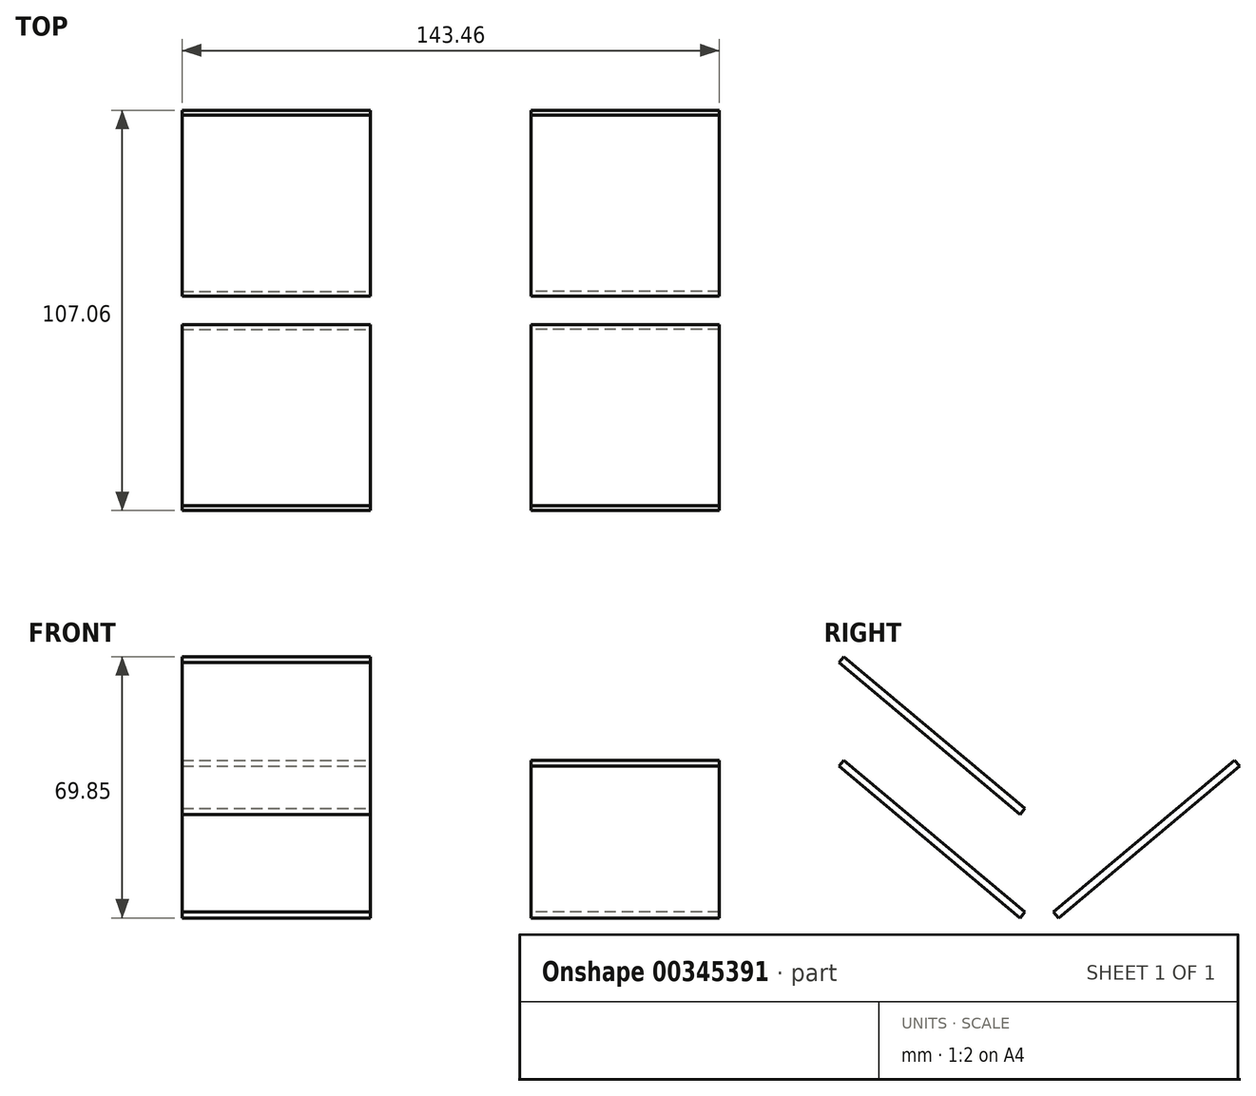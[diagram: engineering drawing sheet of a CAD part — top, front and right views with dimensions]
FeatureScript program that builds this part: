
annotation { "Feature Type Name" : "Feature", "Feature Type Description" : "" }
export const myFeature = defineFeature(function(context is Context, id is Id, definition is map)
    precondition{}
    {
        {
            var Q0;
            Q0=qCreatedBy(makeId("Front.planeOp"),FACE);
            var sketch = newSketch(context, id + "F0", { "sketchPlane" : qUnion([Q0])});
            skLineSegment(sketch, "E0.bottom", {"start": v(-65.55, 59.22) * mm, "end": v(7.51, 59.22) * mm});
            skLineSegment(sketch, "E0.top", {"start": v(-65.55, -49.88) * mm, "end": v(7.51, -49.88) * mm});
            skLineSegment(sketch, "E0.left", {"start": v(-65.55, 59.22) * mm, "end": v(-65.55, -49.88) * mm});
            skLineSegment(sketch, "E0.right", {"start": v(7.51, 59.22) * mm, "end": v(7.51, -49.88) * mm});
            skSolve(sketch);
        }
        {
            var Q0;
            Q0=makeQuery(id+"F0.imprint","IMPRINT",FACE,{"disambiguationData":[TD([[makeQuery(id+"F0.imprint","IMPRINT",EDGE,{"derivedFrom":sQuery(id+"F0.wireOp",EDGE,"E0.bottom")}),-1.0]])]});
            extrude(context, id + "F1", {"entities" : qUnion([Q0]), "depth" : 1.52 * mm});
        }
        {
            var Q0;
            Q0=makeQuery(id+"F1.opExtrude","SWEPT_BODY",BODY,{"disambiguationData":[OSD([sQuery(id+"F0.wireOp",EDGE,"E0.bottom"),sQuery(id+"F0.wireOp",EDGE,"E0.top"),sQuery(id+"F0.wireOp",EDGE,"E0.left"),sQuery(id+"F0.wireOp",EDGE,"E0.right")])]});
            deleteBodies(context, id + "F2", {"entities" : qUnion([Q0])});
        }
        {
            var Q0;
            Q0=qCreatedBy(makeId("Top.planeOp"),FACE);
            var sketch = newSketch(context, id + "F3", { "sketchPlane" : qUnion([Q0])});
            skLineSegment(sketch, "E1.bottom", {"start": v(-71.73, 67) * mm, "end": v(-21.47, 67) * mm});
            skLineSegment(sketch, "E1.top", {"start": v(-71.73, 3.82) * mm, "end": v(-21.47, 3.82) * mm});
            skLineSegment(sketch, "E1.left", {"start": v(-71.73, 67) * mm, "end": v(-71.73, 3.82) * mm});
            skLineSegment(sketch, "E1.right", {"start": v(-21.47, 67) * mm, "end": v(-21.47, 3.82) * mm});
            skSolve(sketch);
        }
        {
            var Q0;
            Q0=makeQuery(id+"F3.imprint","IMPRINT",FACE,{"disambiguationData":[TD([[makeQuery(id+"F3.imprint","IMPRINT",EDGE,{"derivedFrom":sQuery(id+"F3.wireOp",EDGE,"E1.bottom")}),-1.0]])]});
            extrude(context, id + "F4", {"entities" : qUnion([Q0]), "depth" : 2.03 * mm});
        }
        {
            var Q0;
            Q0=makeQuery(id+"F4.opExtrude","SWEPT_BODY",BODY,{"disambiguationData":[OSD([sQuery(id+"F3.wireOp",EDGE,"E1.bottom"),sQuery(id+"F3.wireOp",EDGE,"E1.top"),sQuery(id+"F3.wireOp",EDGE,"E1.left"),sQuery(id+"F3.wireOp",EDGE,"E1.right")])]});
            var Q1;
            Q1=qCreatedBy(makeId("Right.planeOp"),FACE);
            mirror(context, id + "F5", {"entities" : qUnion([Q0]), "mirrorPlane" : qUnion([Q1])});
        }
        {
            var Q0;
            Q0=makeQuery(id+"F4.opExtrude","SWEPT_BODY",BODY,{"disambiguationData":[OSD([sQuery(id+"F3.wireOp",EDGE,"E1.bottom"),sQuery(id+"F3.wireOp",EDGE,"E1.top"),sQuery(id+"F3.wireOp",EDGE,"E1.left"),sQuery(id+"F3.wireOp",EDGE,"E1.right")])]});
            var Q1;
            Q1=makeQuery(id+"F5.opPattern","COPY",BODY,{"derivedFrom":makeQuery(id+"F4.opExtrude","SWEPT_BODY",BODY,{"disambiguationData":[OSD([sQuery(id+"F3.wireOp",EDGE,"E1.bottom"),sQuery(id+"F3.wireOp",EDGE,"E1.top"),sQuery(id+"F3.wireOp",EDGE,"E1.left"),sQuery(id+"F3.wireOp",EDGE,"E1.right")])]}),"instanceName":"1"});
            var Q2;
            Q2=qCreatedBy(makeId("Front.planeOp"),FACE);
            mirror(context, id + "F6", {"entities" : qUnion([Q0, Q1]), "mirrorPlane" : qUnion([Q2])});
        }
        {
            var Q0;
            Q0=makeQuery(id+"F4.opExtrude","SWEPT_BODY",BODY,{"disambiguationData":[OSD([sQuery(id+"F3.wireOp",EDGE,"E1.bottom"),sQuery(id+"F3.wireOp",EDGE,"E1.top"),sQuery(id+"F3.wireOp",EDGE,"E1.left"),sQuery(id+"F3.wireOp",EDGE,"E1.right")])]});
            var Q1;
            Q1=makeQuery(id+"F4.opExtrude","CAP_EDGE",EDGE,{"disambiguationData":[OSD([sQuery(id+"F3.wireOp",EDGE,"E1.top")])],"isStart":false});
            transform(context, id + "F7", {"entities" : qUnion([Q0]), "transformType" : TransformType.ROTATION, "transformAxis" : qUnion([Q1]), "angle" : 40 * degree, "makeCopy" : false});
        }
        {
            var Q0;
            Q0=makeQuery(id+"F6.opPattern","COPY",BODY,{"derivedFrom":makeQuery(id+"F5.opPattern","COPY",BODY,{"derivedFrom":makeQuery(id+"F4.opExtrude","SWEPT_BODY",BODY,{"disambiguationData":[OSD([sQuery(id+"F3.wireOp",EDGE,"E1.bottom"),sQuery(id+"F3.wireOp",EDGE,"E1.top"),sQuery(id+"F3.wireOp",EDGE,"E1.left"),sQuery(id+"F3.wireOp",EDGE,"E1.right")])]}),"instanceName":"1"}),"instanceName":"1"});
            var Q1;
            Q1=makeQuery(id+"F6.opPattern","COPY",EDGE,{"derivedFrom":makeQuery(id+"F4.opExtrude","CAP_EDGE",EDGE,{"disambiguationData":[OSD([sQuery(id+"F3.wireOp",EDGE,"E1.top")])],"isStart":false}),"instanceName":"1"});
            transform(context, id + "F8", {"entities" : qUnion([Q0]), "transformType" : TransformType.ROTATION, "transformAxis" : qUnion([Q1]), "angle" : 40 * degree, "oppositeDirection" : true, "makeCopy" : false});
        }
        {
            var Q0;
            Q0=makeQuery(id+"F6.opPattern","COPY",BODY,{"derivedFrom":makeQuery(id+"F4.opExtrude","SWEPT_BODY",BODY,{"disambiguationData":[OSD([sQuery(id+"F3.wireOp",EDGE,"E1.bottom"),sQuery(id+"F3.wireOp",EDGE,"E1.top"),sQuery(id+"F3.wireOp",EDGE,"E1.left"),sQuery(id+"F3.wireOp",EDGE,"E1.right")])]}),"instanceName":"1"});
            var Q1;
            Q1=makeQuery(id+"F6.opPattern","COPY",EDGE,{"derivedFrom":makeQuery(id+"F4.opExtrude","CAP_EDGE",EDGE,{"disambiguationData":[OSD([sQuery(id+"F3.wireOp",EDGE,"E1.top")])],"isStart":false}),"instanceName":"1"});
            transform(context, id + "F9", {"entities" : qUnion([Q0]), "transformType" : TransformType.ROTATION, "transformAxis" : qUnion([Q1]), "angle" : 40 * degree, "oppositeDirection" : true, "makeCopy" : false});
        }
        {
            var Q0;
            Q0=makeQuery(id+"F5.opPattern","COPY",BODY,{"derivedFrom":makeQuery(id+"F4.opExtrude","SWEPT_BODY",BODY,{"disambiguationData":[OSD([sQuery(id+"F3.wireOp",EDGE,"E1.bottom"),sQuery(id+"F3.wireOp",EDGE,"E1.top"),sQuery(id+"F3.wireOp",EDGE,"E1.left"),sQuery(id+"F3.wireOp",EDGE,"E1.right")])]}),"instanceName":"1"});
            var Q1;
            Q1=makeQuery(id+"F5.opPattern","COPY",EDGE,{"derivedFrom":makeQuery(id+"F4.opExtrude","CAP_EDGE",EDGE,{"disambiguationData":[OSD([sQuery(id+"F3.wireOp",EDGE,"E1.top")])],"isStart":false}),"instanceName":"1"});
            transform(context, id + "F10", {"entities" : qUnion([Q0]), "transformType" : TransformType.ROTATION, "transformAxis" : qUnion([Q1]), "angle" : 40 * degree, "oppositeDirection" : true, "makeCopy" : false});
        }
        {
            var Q0;
            Q0=makeQuery(id+"F6.opPattern","COPY",BODY,{"derivedFrom":makeQuery(id+"F4.opExtrude","SWEPT_BODY",BODY,{"disambiguationData":[OSD([sQuery(id+"F3.wireOp",EDGE,"E1.bottom"),sQuery(id+"F3.wireOp",EDGE,"E1.top"),sQuery(id+"F3.wireOp",EDGE,"E1.left"),sQuery(id+"F3.wireOp",EDGE,"E1.right")])]}),"instanceName":"1"});
            var Q1;
            Q1=qCreatedBy(makeId("Top.planeOp"),FACE);
            var Q2;
            Q2=qCreatedBy(makeId("Right.planeOp"),FACE);
            transform(context, id + "F11", {"entities" : qUnion([Q0]), "transformType" : TransformType.TRANSLATION_DISTANCE, "transformDirection" : qUnion([Q1, Q2]), "distance" : 27.7 * mm, "makeCopy" : false});
        }
    });
